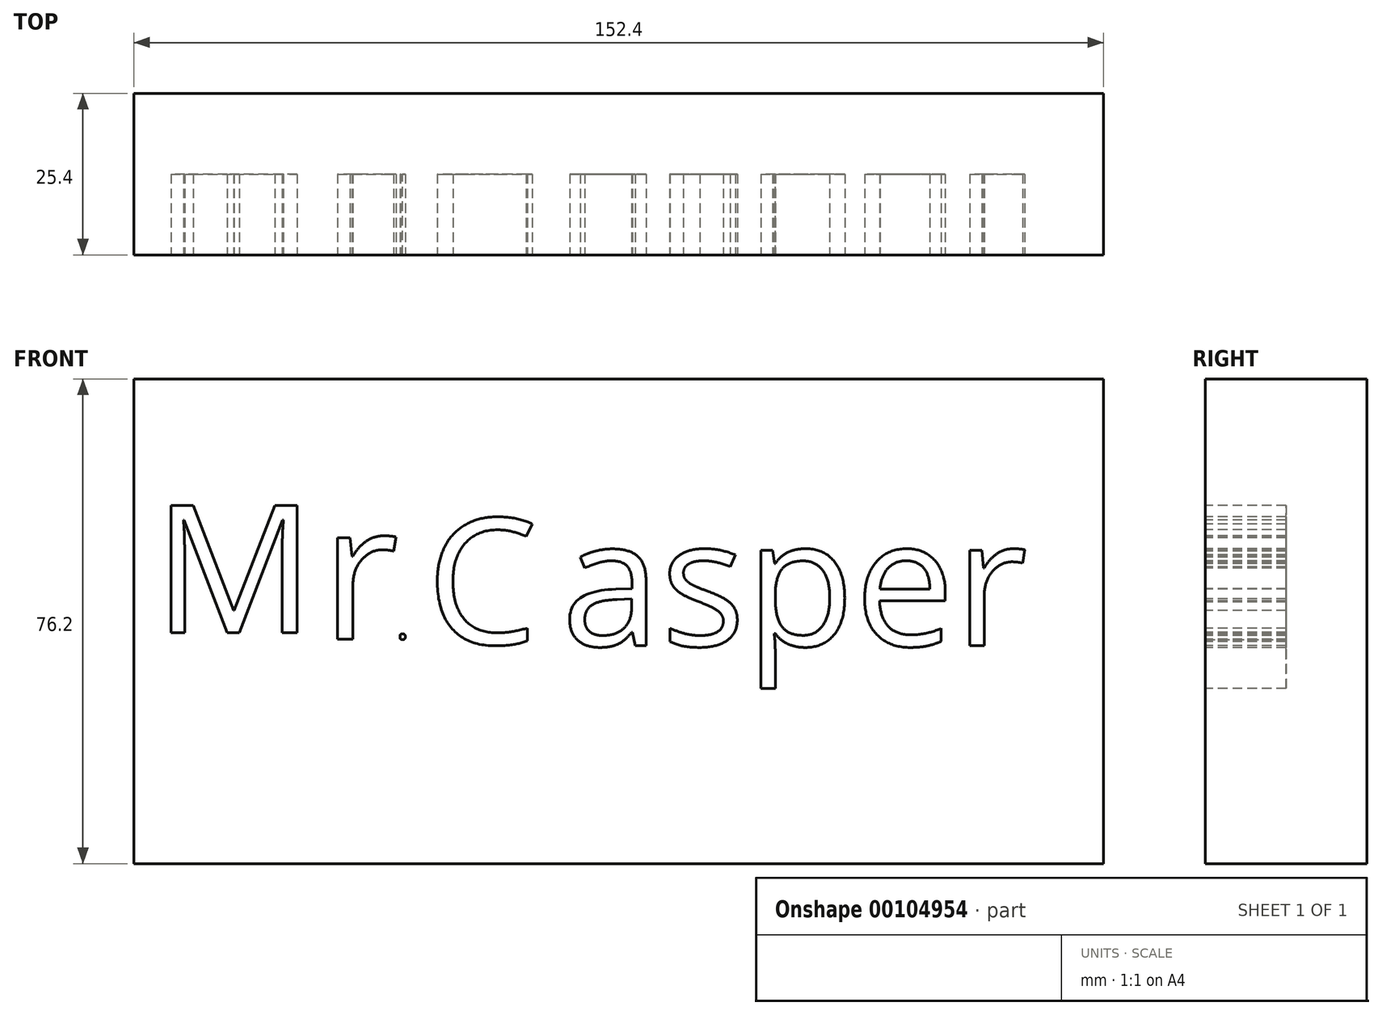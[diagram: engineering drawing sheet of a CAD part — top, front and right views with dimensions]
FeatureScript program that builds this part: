
annotation { "Feature Type Name" : "Feature", "Feature Type Description" : "" }
export const myFeature = defineFeature(function(context is Context, id is Id, definition is map)
    precondition{}
    {
        {
            var Q0;
            Q0=qCreatedBy(makeId("Front.planeOp"),FACE);
            var sketch = newSketch(context, id + "F0", { "sketchPlane" : qUnion([Q0])});
            skLineSegment(sketch, "E0", {"start": v(75.6, 0) * mm, "end": v(-76.8, 0) * mm});
            skLineSegment(sketch, "E1", {"start": v(-76.8, 0) * mm, "end": v(-76.8, 76.2) * mm});
            skLineSegment(sketch, "E2", {"start": v(-76.8, 76.2) * mm, "end": v(75.6, 76.2) * mm});
            skLineSegment(sketch, "E3", {"start": v(75.6, 76.2) * mm, "end": v(75.6, 0) * mm});
            skSolve(sketch);
        }
        {
            var Q0;
            Q0 = qSketchRegion(id + "F0", true);
            extrude(context, id + "F1", {"entities" : qUnion([Q0]), "depth" : 25.4 * mm});
        }
        {
            var Q0;
            Q0=makeQuery(id+"F1.opExtrude","CAP_FACE",FACE,{"disambiguationData":[OSD([sQuery(id+"F0.wireOp",EDGE,"E0"),sQuery(id+"F0.wireOp",EDGE,"E1"),sQuery(id+"F0.wireOp",EDGE,"E2"),sQuery(id+"F0.wireOp",EDGE,"E3")])],"isStart":false});
            var sketch = newSketch(context, id + "F2", { "sketchPlane" : qUnion([Q0])});
            skText(sketch, "E4", { "text": "M", "fontName": "OpenSans-Regular.ttf"});
            skText(sketch, "E5", { "text": "C", "fontName": "OpenSans-Regular.ttf"});
            skText(sketch, "E6", { "text": "r", "fontName": "OpenSans-Regular.ttf"});
            skText(sketch, "E7", { "text": "asper", "fontName": "OpenSans-Regular.ttf"});
            skText(sketch, "E8", { "text": ".", "fontName": "OpenSans-Regular.ttf"});
            const initialGuessF2  = {"E4": [-0.07372, 0.03632, 1, 0, 0.02016], "E5": [-0.0308, 0.03451, 1, 0, 0.0199], "E6": [-0.04735, 0.03529, 1, 0, 0.02146], "E7": [-0.0096, 0.03425, 1, 0, 0.02016], "E8": [-0.03552, 0.03529, 1, 0, 0.00517]};
            skSetInitialGuess(sketch, initialGuessF2);
            skSolve(sketch);
        }
        {
            var Q0;
            Q0 = qSketchRegion(id + "F2", true);
            extrude(context, id + "F3", {"entities" : qUnion([Q0]), "operationType" : NewBodyOperationType.REMOVE, "oppositeDirection" : true, "depth" : 12.7 * mm});
        }
    });
